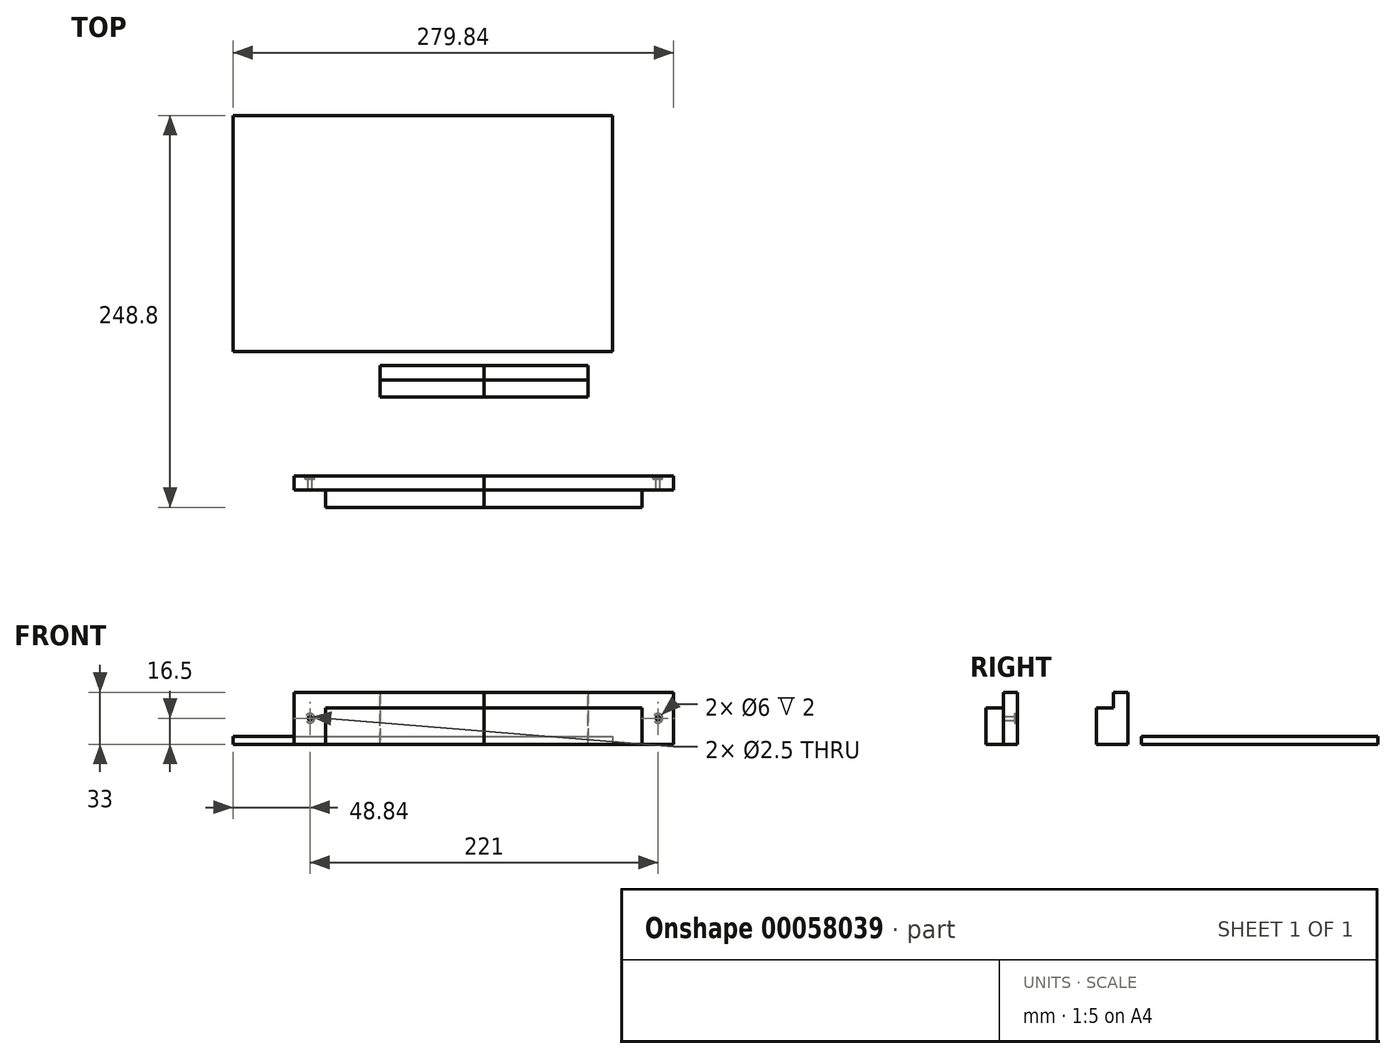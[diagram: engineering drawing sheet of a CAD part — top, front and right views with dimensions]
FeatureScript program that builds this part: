
annotation { "Feature Type Name" : "Feature", "Feature Type Description" : "" }
export const myFeature = defineFeature(function(context is Context, id is Id, definition is map)
    precondition{}
    {
        {
            var Q0;
            Q0=qCreatedBy(makeId("Top.planeOp"),FACE);
            var sketch = newSketch(context, id + "F0", { "sketchPlane" : qUnion([Q0])});
            skLineSegment(sketch, "E0.bottom", {"start": v(-159.34, 113.4) * mm, "end": v(81.66, 113.4) * mm});
            skLineSegment(sketch, "E0.top", {"start": v(-159.34, -36.6) * mm, "end": v(81.66, -36.6) * mm});
            skLineSegment(sketch, "E0.left", {"start": v(-159.34, 113.4) * mm, "end": v(-159.34, -36.6) * mm});
            skLineSegment(sketch, "E0.right", {"start": v(81.66, 113.4) * mm, "end": v(81.66, -36.6) * mm});
            skSolve(sketch);
        }
        {
            var Q0;
            Q0 = qSketchRegion(id + "F0", true);
            var Q1;
            Q1=makeQuery(id+"F0.imprint","IMPRINT",FACE,{"disambiguationData":[TD([[makeQuery(id+"F0.imprint","IMPRINT",EDGE,{"derivedFrom":sQuery(id+"F0.wireOp",EDGE,"E0.bottom")}),-1.0]])]});
            extrude(context, id + "F1", {"entities" : qUnion([Q0, Q1]), "depth" : 5 * mm});
        }
        {
            var Q0;
            Q0=qCreatedBy(makeId("Right.planeOp"),FACE);
            var sketch = newSketch(context, id + "F2", { "sketchPlane" : qUnion([Q0])});
            skLineSegment(sketch, "E1", {"start": v(-115.41, 0) * mm, "end": v(-115.41, 33) * mm});
            skLineSegment(sketch, "E2", {"start": v(-115.41, 33) * mm, "end": v(-124.41, 33) * mm});
            skLineSegment(sketch, "E3", {"start": v(-124.41, 33) * mm, "end": v(-124.41, 23) * mm});
            skLineSegment(sketch, "E4", {"start": v(-124.41, 23) * mm, "end": v(-135.41, 23) * mm});
            skLineSegment(sketch, "E5", {"start": v(-135.41, 23) * mm, "end": v(-135.41, 0) * mm});
            skLineSegment(sketch, "E6", {"start": v(-135.41, 0) * mm, "end": v(-115.41, 0) * mm});
            skSolve(sketch);
        }
        {
            var Q0;
            Q0=makeQuery(id+"F2.imprint","IMPRINT",FACE,{"disambiguationData":[TD([[makeQuery(id+"F2.imprint","IMPRINT",EDGE,{"derivedFrom":sQuery(id+"F2.wireOp",EDGE,"E1")}),1.0]])]});
            extrude(context, id + "F3", {"entities" : qUnion([Q0]), "depth" : 120.5 * mm});
        }
        {
            var Q0;
            Q0=makeQuery(id+"F3.opExtrude","SWEPT_FACE",FACE,{"disambiguationData":[OSD([sQuery(id+"F2.wireOp",EDGE,"E4")])]});
            var sketch = newSketch(context, id + "F4", { "sketchPlane" : qUnion([Q0])});
            skLineSegment(sketch, "E7.bottom", {"start": v(120.5, -135.41) * mm, "end": v(100.5, -135.41) * mm});
            skLineSegment(sketch, "E7.top", {"start": v(120.5, -124.41) * mm, "end": v(100.5, -124.41) * mm});
            skLineSegment(sketch, "E7.left", {"start": v(120.5, -135.41) * mm, "end": v(120.5, -124.41) * mm});
            skLineSegment(sketch, "E7.right", {"start": v(100.5, -135.41) * mm, "end": v(100.5, -124.41) * mm});
            skSolve(sketch);
        }
        {
            var Q0;
            Q0=makeQuery(id+"F4.imprint","IMPRINT",FACE,{"disambiguationData":[TD([[makeQuery(id+"F4.imprint","IMPRINT",EDGE,{"derivedFrom":sQuery(id+"F4.wireOp",EDGE,"E7.bottom")}),-1.0]])]});
            extrude(context, id + "F5", {"entities" : qUnion([Q0]), "operationType" : NewBodyOperationType.REMOVE, "endBound" : BoundingType.THROUGH_ALL, "oppositeDirection" : true, "depth" : 25 * mm});
        }
        {
            var Q0;
            Q0=qCreatedBy(makeId("Right.planeOp"),FACE);
            var sketch = newSketch(context, id + "F6", { "sketchPlane" : qUnion([Q0])});
            skLineSegment(sketch, "E8", {"start": v(-45.46, 0) * mm, "end": v(-65.46, 0) * mm});
            skLineSegment(sketch, "E9", {"start": v(-65.46, 0) * mm, "end": v(-65.46, 23) * mm});
            skLineSegment(sketch, "E10", {"start": v(-65.46, 23) * mm, "end": v(-54.46, 23) * mm});
            skLineSegment(sketch, "E11", {"start": v(-54.46, 23) * mm, "end": v(-54.46, 33) * mm});
            skLineSegment(sketch, "E12", {"start": v(-54.46, 33) * mm, "end": v(-45.46, 33) * mm});
            skLineSegment(sketch, "E13", {"start": v(-45.46, 33) * mm, "end": v(-45.46, 0) * mm});
            skSolve(sketch);
        }
        {
            var Q0;
            Q0=makeQuery(id+"F6.imprint","IMPRINT",FACE,{"disambiguationData":[TD([[makeQuery(id+"F6.imprint","IMPRINT",EDGE,{"derivedFrom":sQuery(id+"F6.wireOp",EDGE,"E8")}),-1.0]])]});
            extrude(context, id + "F7", {"entities" : qUnion([Q0]), "depth" : 66 * mm});
        }
        {
            var Q0;
            Q0=makeQuery(id+"F7.opExtrude","SWEPT_BODY",BODY,{"disambiguationData":[OSD([sQuery(id+"F6.wireOp",EDGE,"E8"),sQuery(id+"F6.wireOp",EDGE,"E9"),sQuery(id+"F6.wireOp",EDGE,"E10"),sQuery(id+"F6.wireOp",EDGE,"E11"),sQuery(id+"F6.wireOp",EDGE,"E12"),sQuery(id+"F6.wireOp",EDGE,"E13")])]});
            var Q1;
            Q1=qCreatedBy(makeId("Right.planeOp"),FACE);
            mirror(context, id + "F8", {"operationType" : NewBodyOperationType.ADD, "entities" : qUnion([Q0]), "mirrorPlane" : qUnion([Q1])});
        }
        {
            var Q0;
            Q0=makeQuery(id+"F3.opExtrude","SWEPT_FACE",FACE,{"disambiguationData":[OSD([sQuery(id+"F2.wireOp",EDGE,"E1")])]});
            var sketch = newSketch(context, id + "F9", { "sketchPlane" : qUnion([Q0])});
            skCircle(sketch, "E14", {"center": v(-110.5, 16.5) * mm, "radius": 3 * mm});
            skSolve(sketch);
        }
        {
            var Q0;
            Q0 = qSketchRegion(id + "F9", true);
            extrude(context, id + "F10", {"entities" : qUnion([Q0]), "operationType" : NewBodyOperationType.REMOVE, "oppositeDirection" : true, "depth" : 2 * mm});
        }
        {
            var Q0;
            Q0=makeQuery(id+"F10.boolean.opBoolean","COPY",FACE,{"derivedFrom":makeQuery(id+"F10.opExtrude","CAP_FACE",FACE,{"disambiguationData":[OSD([sQuery(id+"F9.wireOp",EDGE,"E14")])],"isStart":false})});
            var sketch = newSketch(context, id + "F11", { "sketchPlane" : qUnion([Q0])});
            skCircle(sketch, "E15", {"center": v(-110.5, 16.5) * mm, "radius": 1.25 * mm});
            skSolve(sketch);
        }
        {
            var Q0;
            Q0 = qSketchRegion(id + "F11", true);
            extrude(context, id + "F12", {"entities" : qUnion([Q0]), "operationType" : NewBodyOperationType.REMOVE, "endBound" : BoundingType.THROUGH_ALL, "oppositeDirection" : true, "depth" : 25 * mm});
        }
        {
            var Q0;
            Q0=makeQuery(id+"F3.opExtrude","SWEPT_BODY",BODY,{"disambiguationData":[OSD([sQuery(id+"F2.wireOp",EDGE,"E1"),sQuery(id+"F2.wireOp",EDGE,"E2"),sQuery(id+"F2.wireOp",EDGE,"E3"),sQuery(id+"F2.wireOp",EDGE,"E4"),sQuery(id+"F2.wireOp",EDGE,"E5"),sQuery(id+"F2.wireOp",EDGE,"E6")])]});
            var Q1;
            Q1=qCreatedBy(makeId("Right.planeOp"),FACE);
            mirror(context, id + "F13", {"operationType" : NewBodyOperationType.ADD, "entities" : qUnion([Q0]), "mirrorPlane" : qUnion([Q1])});
        }
    });
